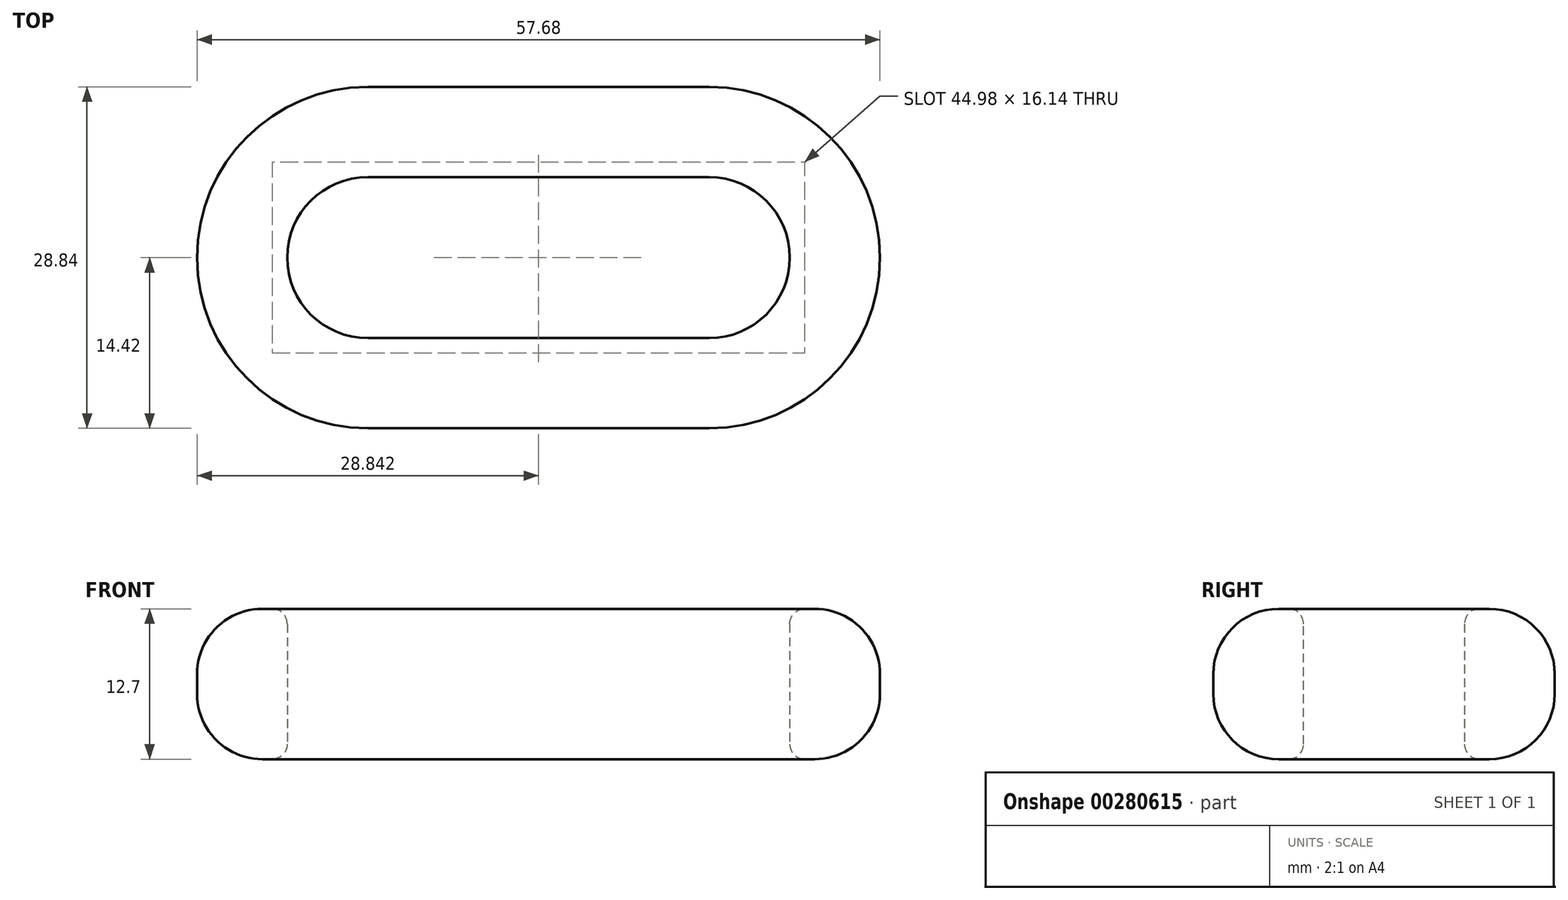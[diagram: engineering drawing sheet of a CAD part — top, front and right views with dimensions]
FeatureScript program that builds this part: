
annotation { "Feature Type Name" : "Feature", "Feature Type Description" : "" }
export const myFeature = defineFeature(function(context is Context, id is Id, definition is map)
    precondition{}
    {
        {
            var Q0;
            Q0=qCreatedBy(makeId("Top.planeOp"),FACE);
            var sketch = newSketch(context, id + "F0", { "sketchPlane" : qUnion([Q0])});
            skLineSegment(sketch, "E0.bottom", {"start": v(0, 0) * mm, "end": v(28.84, 0) * mm});
            skLineSegment(sketch, "E0.top", {"start": v(0, -28.84) * mm, "end": v(28.84, -28.84) * mm});
            skLineSegment(sketch, "E0.left", {"start": v(0, 0) * mm, "end": v(0, -28.84) * mm});
            skLineSegment(sketch, "E0.right", {"start": v(28.84, 0) * mm, "end": v(28.84, -28.84) * mm});
            skCircle(sketch, "E1", {"center": v(28.84, -14.42) * mm, "radius": 14.42 * mm});
            skCircle(sketch, "E2", {"center": v(0, -14.42) * mm, "radius": 14.42 * mm});
            skSolve(sketch);
        }
        {
            var Q0;
            {var subQ0=sQuery(id+"F0.wireOp",EDGE,"E0.left");Q0=makeQuery(id+"F0.imprint","IMPRINT",FACE,{"disambiguationData":[TD([[makeQuery(id+"F0.imprint","IMPRINT",EDGE,{"derivedFrom":subQ0}),-1.0]])]});}
            var Q1;
            {var subQ0=sQuery(id+"F0.wireOp",EDGE,"E0.right");Q1=makeQuery(id+"F0.imprint","IMPRINT",FACE,{"disambiguationData":[TD([[makeQuery(id+"F0.imprint","IMPRINT",EDGE,{"derivedFrom":subQ0}),1.0]])]});}
            var Q2;
            {var subQ0=sQuery(id+"F0.wireOp",EDGE,"E0.bottom");Q2=makeQuery(id+"F0.imprint","IMPRINT",FACE,{"disambiguationData":[TD([[makeQuery(id+"F0.imprint","IMPRINT",EDGE,{"derivedFrom":subQ0}),-1.0]])]});}
            var Q3;
            {var subQ0=sQuery(id+"F0.wireOp",EDGE,"E0.left");Q3=makeQuery(id+"F0.imprint","IMPRINT",FACE,{"disambiguationData":[TD([[makeQuery(id+"F0.imprint","IMPRINT",EDGE,{"derivedFrom":subQ0}),1.0]])]});}
            var Q4;
            {var subQ0=sQuery(id+"F0.wireOp",EDGE,"E0.right");Q4=makeQuery(id+"F0.imprint","IMPRINT",FACE,{"disambiguationData":[TD([[makeQuery(id+"F0.imprint","IMPRINT",EDGE,{"derivedFrom":subQ0}),-1.0]])]});}
            extrude(context, id + "F1", {"entities" : qUnion([Q0, Q1, Q2, Q3, Q4]), "depth" : 12.7 * mm});
        }
        {
            var Q0;
            Q0=makeQuery(id+"F1.opExtrude","CAP_FACE",FACE,{"disambiguationData":[OSD([sQuery(id+"F0.wireOp",EDGE,"E0.bottom"),sQuery(id+"F0.wireOp",EDGE,"E0.top"),sQuery(id+"F0.wireOp",EDGE,"E1"),sQuery(id+"F0.wireOp",EDGE,"E2")])],"isStart":false});
            var Q1;
            Q1=makeQuery(id+"F1.opExtrude","CAP_FACE",FACE,{"disambiguationData":[OSD([sQuery(id+"F0.wireOp",EDGE,"E0.bottom"),sQuery(id+"F0.wireOp",EDGE,"E0.top"),sQuery(id+"F0.wireOp",EDGE,"E1"),sQuery(id+"F0.wireOp",EDGE,"E2")])],"isStart":true});
            shell(context, id + "F2", {"entities" : qUnion([Q0, Q1]), "thickness" : 7.62 * mm});
        }
        {
            var Q0;
            Q0=makeQuery(id+"F1.opExtrude","CAP_EDGE",EDGE,{"disambiguationData":[OSD([sQuery(id+"F0.wireOp",EDGE,"E0.top")])],"isStart":false});
            var Q1;
            Q1=makeQuery(id+"F1.opExtrude","CAP_EDGE",EDGE,{"disambiguationData":[OSD([sQuery(id+"F0.wireOp",EDGE,"E0.top")])],"isStart":true});
            fillet(context, id + "F3", {"entities" : qUnion([Q0, Q1]), "radius" : 5.52 * mm, "tangentPropagation" : true, "allowEdgeOverflow" : false});
        }
        {
            var Q0;
            {var subQ0=sQuery(id+"F0.wireOp",EDGE,"E0.bottom");Q0=makeQuery(id+"F2.opShell","OFFSET_EDGE",EDGE,{"disambiguationData":[OSD([subQ0]),TDD([makeQuery(id+"F1.opExtrude","CAP_EDGE",EDGE,{"disambiguationData":[OSD([subQ0])],"isStart":true})])]});}
            var Q1;
            {var subQ0=sQuery(id+"F0.wireOp",EDGE,"E0.bottom");Q1=makeQuery(id+"F2.opShell","OFFSET_EDGE",EDGE,{"disambiguationData":[OSD([subQ0]),TDD([makeQuery(id+"F1.opExtrude","CAP_EDGE",EDGE,{"disambiguationData":[OSD([subQ0])],"isStart":false})])]});}
            fillet(context, id + "F4", {"entities" : qUnion([Q0, Q1]), "radius" : 1.27 * mm, "tangentPropagation" : true, "allowEdgeOverflow" : false});
        }
    });
